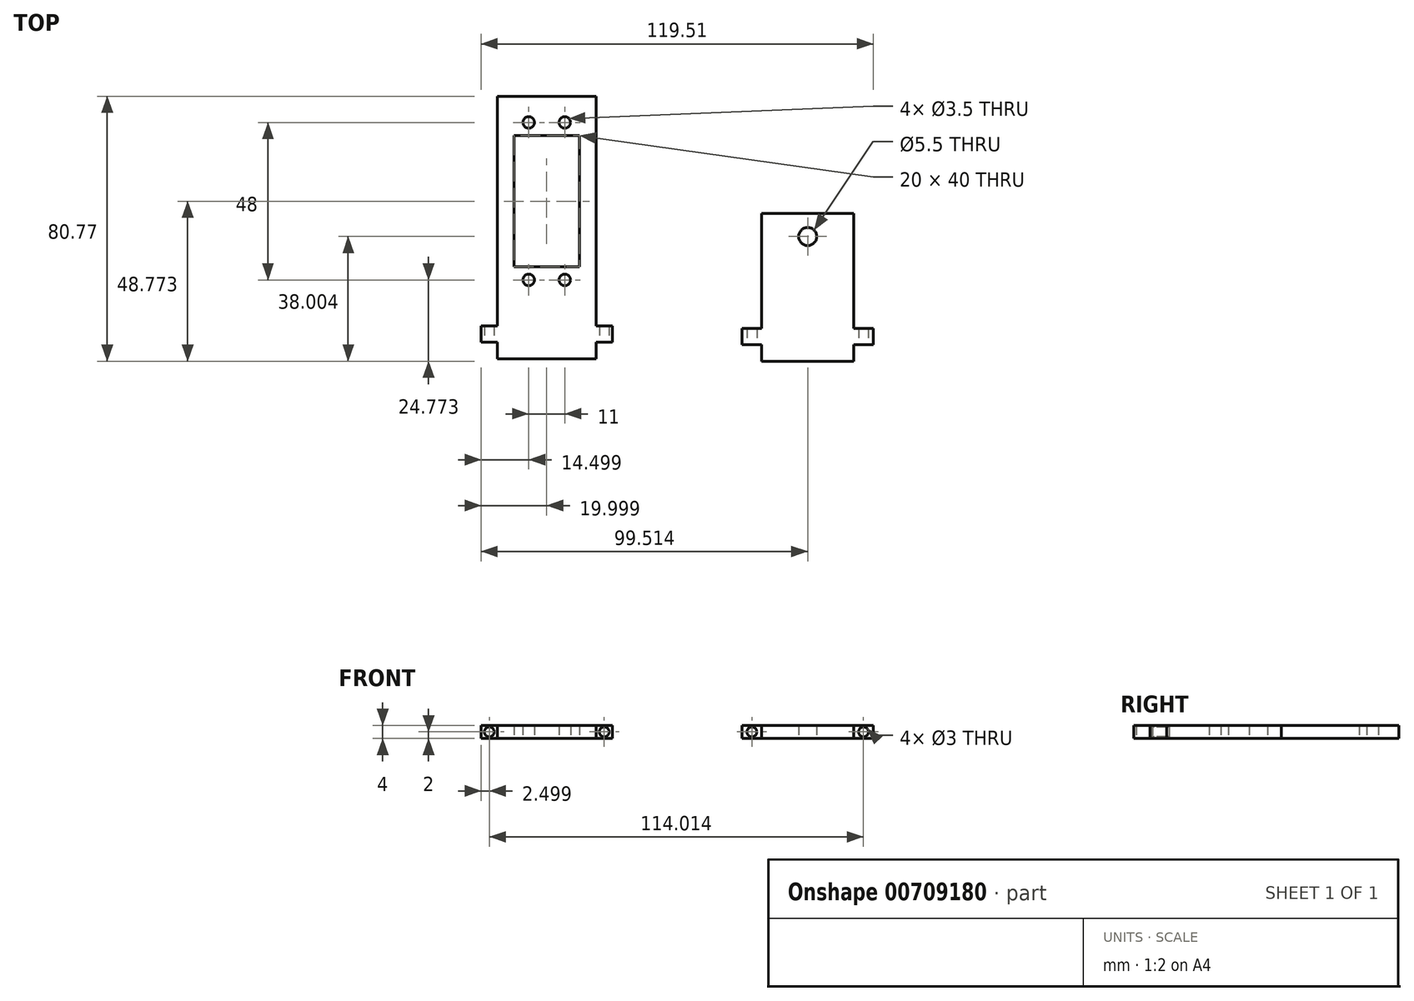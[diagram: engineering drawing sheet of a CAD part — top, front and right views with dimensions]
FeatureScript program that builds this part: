
annotation { "Feature Type Name" : "Feature", "Feature Type Description" : "" }
export const myFeature = defineFeature(function(context is Context, id is Id, definition is map)
    precondition{}
    {
        {
            var Q0;
            Q0=qCreatedBy(makeId("Top.planeOp"),FACE);
            var sketch = newSketch(context, id + "F0", { "sketchPlane" : qUnion([Q0])});
            skLineSegment(sketch, "E0.bottom", {"start": v(-59.15, 47.45) * mm, "end": v(-29.15, 47.45) * mm});
            skLineSegment(sketch, "E0.top", {"start": v(-59.15, -32.55) * mm, "end": v(-29.15, -32.55) * mm});
            skLineSegment(sketch, "E0.left", {"start": v(-59.15, 47.45) * mm, "end": v(-59.15, -32.55) * mm});
            skLineSegment(sketch, "E0.right", {"start": v(-29.15, 47.45) * mm, "end": v(-29.15, -32.55) * mm});
            skLineSegment(sketch, "E1.bottom", {"start": v(-64.15, -22.55) * mm, "end": v(-24.15, -22.55) * mm});
            skLineSegment(sketch, "E1.top", {"start": v(-64.15, -27.55) * mm, "end": v(-24.15, -27.55) * mm});
            skLineSegment(sketch, "E1.left", {"start": v(-64.15, -22.55) * mm, "end": v(-64.15, -27.55) * mm});
            skLineSegment(sketch, "E1.right", {"start": v(-24.15, -22.55) * mm, "end": v(-24.15, -27.55) * mm});
            skLineSegment(sketch, "E2.bottom", {"start": v(-54.15, 35.45) * mm, "end": v(-34.15, 35.45) * mm});
            skLineSegment(sketch, "E2.top", {"start": v(-54.15, -4.55) * mm, "end": v(-34.15, -4.55) * mm});
            skLineSegment(sketch, "E2.left", {"start": v(-54.15, 35.45) * mm, "end": v(-54.15, -4.55) * mm});
            skLineSegment(sketch, "E2.right", {"start": v(-34.15, 35.45) * mm, "end": v(-34.15, -4.55) * mm});
            skPoint(sketch, "E3", {"position": v(-49.65, -8.55) * mm});
            skPoint(sketch, "E4", {"position": v(-38.65, -8.55) * mm});
            skPoint(sketch, "E5.MirrorP", {"position": v(-38.65, 39.45) * mm});
            skPoint(sketch, "E6.MirrorP", {"position": v(-49.65, 39.45) * mm});
            skSolve(sketch);
        }
        {
            var Q0;
            {var subQ0=sQuery(id+"F0.wireOp",EDGE,"E0.bottom");Q0=makeQuery(id+"F0.imprint","IMPRINT",FACE,{"disambiguationData":[TD([[makeQuery(id+"F0.imprint","IMPRINT",EDGE,{"derivedFrom":subQ0}),-1.0]])]});}
            var Q1;
            {var subQ0=sQuery(id+"F0.wireOp",EDGE,"E1.bottom");var subQ1=sQuery(id+"F0.wireOp",EDGE,"E0.left");var subQ2=makeQuery(id+"F0.imprint","INTERSECT",VERTEX,{"derivedFrom":[subQ1,subQ0]});Q1=makeQuery(id+"F0.imprint","IMPRINT",FACE,{"disambiguationData":[TD([[makeQuery(id+"F0.imprint","IMPRINT",EDGE,{"disambiguationData":[TD([[subQ2,-1.0]])],"derivedFrom":subQ1}),1.0]])]});}
            var Q2;
            {var subQ5=sQuery(id+"F0.wireOp",EDGE,"E1.left");Q2=makeQuery(id+"F0.imprint","IMPRINT",FACE,{"disambiguationData":[TD([[makeQuery(id+"F0.imprint","IMPRINT",EDGE,{"derivedFrom":subQ5}),1.0]])]});}
            var Q3;
            {var subQ0=sQuery(id+"F0.wireOp",EDGE,"E0.top");Q3=makeQuery(id+"F0.imprint","IMPRINT",FACE,{"disambiguationData":[TD([[makeQuery(id+"F0.imprint","IMPRINT",EDGE,{"derivedFrom":subQ0}),1.0]])]});}
            var Q4;
            {var subQ5=sQuery(id+"F0.wireOp",EDGE,"E1.right");Q4=makeQuery(id+"F0.imprint","IMPRINT",FACE,{"disambiguationData":[TD([[makeQuery(id+"F0.imprint","IMPRINT",EDGE,{"derivedFrom":subQ5}),-1.0]])]});}
            extrude(context, id + "F1", {"entities" : qUnion([Q0, Q1, Q2, Q3, Q4]), "depth" : 4 * mm, "offsetDistance" : 25 * mm});
        }
        {
            var Q0;
            {var subQ0=sQuery(id+"F0.wireOp",EDGE,"E1.top");Q0=makeQuery(id+"F1.opExtrude","SWEPT_FACE",FACE,{"disambiguationData":[OSD([subQ0]),TDD([makeQuery(id+"F0.imprint","IMPRINT",EDGE,{"disambiguationData":[TD([[makeQuery(id+"F0.imprint","INTERSECT",VERTEX,{"derivedFrom":[subQ0,sQuery(id+"F0.wireOp",EDGE,"E1.left")]}),-1.0]])],"derivedFrom":subQ0})])]});}
            var sketch = newSketch(context, id + "F2", { "sketchPlane" : qUnion([Q0])});
            skPoint(sketch, "E7", {"position": v(-61.65, 2) * mm});
            skSolve(sketch);
        }
        {
            var Q0;
            {var subQ0=sQuery(id+"F0.wireOp",EDGE,"E1.top");Q0=makeQuery(id+"F1.opExtrude","SWEPT_FACE",FACE,{"disambiguationData":[OSD([subQ0]),TDD([makeQuery(id+"F0.imprint","IMPRINT",EDGE,{"disambiguationData":[TD([[makeQuery(id+"F0.imprint","INTERSECT",VERTEX,{"derivedFrom":[subQ0,sQuery(id+"F0.wireOp",EDGE,"E1.right")]}),1.0]])],"derivedFrom":subQ0})])]});}
            var sketch = newSketch(context, id + "F3", { "sketchPlane" : qUnion([Q0])});
            skPoint(sketch, "E8", {"position": v(-26.65, 2) * mm});
            skSolve(sketch);
        }
        {
            var Q0;
            Q0=sQuery(id+"F2.wireOp",VERTEX,"E7");
            var Q1;
            Q1=sQuery(id+"F3.wireOp",VERTEX,"E8");
            var Q2;
            Q2=makeQuery(id+"F1.opExtrude","SWEPT_BODY",BODY,{"disambiguationData":[OSD([sQuery(id+"F0.wireOp",EDGE,"E0.bottom"),sQuery(id+"F0.wireOp",EDGE,"E0.top"),sQuery(id+"F0.wireOp",EDGE,"E0.left"),sQuery(id+"F0.wireOp",EDGE,"E0.right"),sQuery(id+"F0.wireOp",EDGE,"E1.bottom"),sQuery(id+"F0.wireOp",EDGE,"E1.top"),sQuery(id+"F0.wireOp",EDGE,"E1.left"),sQuery(id+"F0.wireOp",EDGE,"E1.right"),sQuery(id+"F0.wireOp",EDGE,"E2.bottom"),sQuery(id+"F0.wireOp",EDGE,"E2.top"),sQuery(id+"F0.wireOp",EDGE,"E2.left"),sQuery(id+"F0.wireOp",EDGE,"E2.right")])]});
            hole(context, id + "F4", {"style" : HoleStyle.SIMPLE, "endStyle" : HoleEndStyle.BLIND, "holeDiameter" : 3 * mm, "majorDiameter" : 5 * mm, "holeDepth" : 20 * mm, "isTappedThrough" : true, "tappedDepth" : 12 * mm, "tapClearance" : 3, "locations" : qUnion([Q0, Q1]), "scope" : qUnion([Q2])});
        }
        {
            var Q0;
            Q0=sQuery(id+"F0.wireOp",VERTEX,"E6.MirrorP");
            var Q1;
            Q1=sQuery(id+"F0.wireOp",VERTEX,"E5.MirrorP");
            var Q2;
            Q2=sQuery(id+"F0.wireOp",VERTEX,"E3");
            var Q3;
            Q3=sQuery(id+"F0.wireOp",VERTEX,"E4");
            var Q4;
            Q4=makeQuery(id+"F1.opExtrude","SWEPT_BODY",BODY,{"disambiguationData":[OSD([sQuery(id+"F0.wireOp",EDGE,"E0.bottom"),sQuery(id+"F0.wireOp",EDGE,"E0.top"),sQuery(id+"F0.wireOp",EDGE,"E0.left"),sQuery(id+"F0.wireOp",EDGE,"E0.right"),sQuery(id+"F0.wireOp",EDGE,"E1.bottom"),sQuery(id+"F0.wireOp",EDGE,"E1.top"),sQuery(id+"F0.wireOp",EDGE,"E1.left"),sQuery(id+"F0.wireOp",EDGE,"E1.right"),sQuery(id+"F0.wireOp",EDGE,"E2.bottom"),sQuery(id+"F0.wireOp",EDGE,"E2.top"),sQuery(id+"F0.wireOp",EDGE,"E2.left"),sQuery(id+"F0.wireOp",EDGE,"E2.right")])]});
            hole(context, id + "F5", {"style" : HoleStyle.SIMPLE, "endStyle" : HoleEndStyle.THROUGH, "oppositeDirection" : true, "holeDiameter" : 3.5 * mm, "majorDiameter" : 5 * mm, "isTappedThrough" : true, "tappedDepth" : 12 * mm, "tapClearance" : 3, "locations" : qUnion([Q0, Q1, Q2, Q3]), "scope" : qUnion([Q4])});
        }
        {
            var Q0;
            Q0=qCreatedBy(makeId("Top.planeOp"),FACE);
            var sketch = newSketch(context, id + "F6", { "sketchPlane" : qUnion([Q0])});
            skLineSegment(sketch, "E9.top", {"start": v(21.36, -33.32) * mm, "end": v(49.36, -33.32) * mm});
            skLineSegment(sketch, "E9.left", {"start": v(21.36, 11.68) * mm, "end": v(21.36, -33.32) * mm});
            skLineSegment(sketch, "E9.right", {"start": v(49.36, 11.68) * mm, "end": v(49.36, -33.32) * mm});
            skLineSegment(sketch, "E10.bottom", {"start": v(15.36, -23.32) * mm, "end": v(55.36, -23.32) * mm});
            skLineSegment(sketch, "E10.top", {"start": v(15.36, -28.32) * mm, "end": v(55.36, -28.32) * mm});
            skLineSegment(sketch, "E10.left", {"start": v(15.36, -23.32) * mm, "end": v(15.36, -28.32) * mm});
            skLineSegment(sketch, "E10.right", {"start": v(55.36, -23.32) * mm, "end": v(55.36, -28.32) * mm});
            skPoint(sketch, "E11", {"position": v(35.36, 4.68) * mm});
            skLineSegment(sketch, "E12", {"start": v(21.36, 11.68) * mm, "end": v(49.36, 11.68) * mm});
            skSolve(sketch);
        }
        {
            var Q0;
            Q0 = qSketchRegion(id + "F6", true);
            extrude(context, id + "F7", {"entities" : qUnion([Q0]), "depth" : 4 * mm, "offsetDistance" : 25 * mm});
        }
        {
            var Q0;
            {var subQ0=sQuery(id+"F6.wireOp",EDGE,"E10.top");Q0=makeQuery(id+"F7.opExtrude","SWEPT_FACE",FACE,{"disambiguationData":[OSD([subQ0]),TDD([makeQuery(id+"F6.imprint","IMPRINT",EDGE,{"disambiguationData":[TD([[makeQuery(id+"F6.imprint","INTERSECT",VERTEX,{"derivedFrom":[subQ0,sQuery(id+"F6.wireOp",EDGE,"E10.left")]}),-1.0]])],"derivedFrom":subQ0})])]});}
            var sketch = newSketch(context, id + "F8", { "sketchPlane" : qUnion([Q0])});
            skPoint(sketch, "E13", {"position": v(18.36, 2) * mm});
            skSolve(sketch);
        }
        {
            var Q0;
            {var subQ0=sQuery(id+"F6.wireOp",EDGE,"E10.top");Q0=makeQuery(id+"F7.opExtrude","SWEPT_FACE",FACE,{"disambiguationData":[OSD([subQ0]),TDD([makeQuery(id+"F6.imprint","IMPRINT",EDGE,{"disambiguationData":[TD([[makeQuery(id+"F6.imprint","INTERSECT",VERTEX,{"derivedFrom":[subQ0,sQuery(id+"F6.wireOp",EDGE,"E10.right")]}),1.0]])],"derivedFrom":subQ0})])]});}
            var sketch = newSketch(context, id + "F9", { "sketchPlane" : qUnion([Q0])});
            skPoint(sketch, "E14", {"position": v(52.36, 2) * mm});
            skSolve(sketch);
        }
        {
            var Q0;
            Q0=sQuery(id+"F8.wireOp",VERTEX,"E13");
            var Q1;
            Q1=sQuery(id+"F9.wireOp",VERTEX,"E14");
            var Q2;
            Q2=makeQuery(id+"F7.opExtrude","SWEPT_BODY",BODY,{"disambiguationData":[OSD([sQuery(id+"F6.wireOp",EDGE,"E9.bottom"),sQuery(id+"F6.wireOp",EDGE,"E9.top"),sQuery(id+"F6.wireOp",EDGE,"E9.left"),sQuery(id+"F6.wireOp",EDGE,"E9.right"),sQuery(id+"F6.wireOp",EDGE,"E10.bottom"),sQuery(id+"F6.wireOp",EDGE,"E10.top"),sQuery(id+"F6.wireOp",EDGE,"E10.left"),sQuery(id+"F6.wireOp",EDGE,"E10.right")])]});
            hole(context, id + "F10", {"style" : HoleStyle.SIMPLE, "endStyle" : HoleEndStyle.BLIND, "holeDiameter" : 3 * mm, "majorDiameter" : 5 * mm, "holeDepth" : 20 * mm, "isTappedThrough" : true, "tappedDepth" : 12 * mm, "tapClearance" : 3, "locations" : qUnion([Q0, Q1]), "scope" : qUnion([Q2])});
        }
        {
            var Q0;
            Q0=sQuery(id+"F6.wireOp",VERTEX,"E11");
            var Q1;
            Q1=makeQuery(id+"F7.opExtrude","SWEPT_BODY",BODY,{"disambiguationData":[OSD([sQuery(id+"F6.wireOp",EDGE,"E9.bottom"),sQuery(id+"F6.wireOp",EDGE,"E9.top"),sQuery(id+"F6.wireOp",EDGE,"E9.left"),sQuery(id+"F6.wireOp",EDGE,"E9.right"),sQuery(id+"F6.wireOp",EDGE,"E10.bottom"),sQuery(id+"F6.wireOp",EDGE,"E10.top"),sQuery(id+"F6.wireOp",EDGE,"E10.left"),sQuery(id+"F6.wireOp",EDGE,"E10.right")])]});
            hole(context, id + "F11", {"style" : HoleStyle.SIMPLE, "endStyle" : HoleEndStyle.BLIND, "oppositeDirection" : true, "holeDiameter" : 5.5 * mm, "majorDiameter" : 5 * mm, "holeDepth" : 20 * mm, "isTappedThrough" : true, "tappedDepth" : 12 * mm, "tapClearance" : 3, "locations" : qUnion([Q0]), "scope" : qUnion([Q1])});
        }
    });
